# Revit family: Sewage_Removal_System-Zoeller-202_Qwik_Jon_Ultima
name_source: partatom
category: Mechanical Equipment
revit_build: Autodesk Revit 2014 (Build: 20130308_1515(x64)
units: mm (PartAtom-declared; Revit-internal decimal feet)

## types (1)
- 202 – 115V/7.0amps/60Hz
    ADA Compliant = Yes
    Amps = 7 A
    CW Connection = Yes
    Cap = Engineered Plastic
    Cetification = cCSAus (pump only)
    Cooling = Oil Filled
    Cord Length = 108"
    Cord Type = UL listed neoprene cord and plug
    Default Elevation = 0"
    Description = Economical sewage systems designed for free-standing or built-in installations.
    Discharge Diameter = 1"
    Frequency = 60 Hz
    Gasket = Closed cell tank gasket; Buna-N pump o-rings
    HW Connection = No
    Hardware = Stainless Steel
    Height = 14 1/2"
    Horse Power = 1/2
    Impeller = Engineered Plastic
    Impeller Type = Non-clogging vortex
    Insulation = Class B
    Length = 9"
    Lower Bearing = Ball bearings
    Manufacturer = Zoeller
    Material = Plastic-Zoeller-Engineered Plastic
    Max Flow Rate = 45 GPM
    Max. Operating Temp. = 130°F (54°C)
    Maximum Head = 30'
    Mechanical Seals = Carbon/ceramic
    Model = Qwik Jon Ultima
    Motor Housing = Cast iron
    Motor Protection = Auto reset thermal overload
    Motor Shaft = AISI 1215
    Operation = Automatic
    Phase = 1 Ph
    Price = Prices may vary. Please consult Manufacturer Representative for most up-to-date price list.
    Product Documentation Link = http://cdn.qleapahead.com
    Product Page URL = http://www.zoellerpumps.com
    Pump Housing = Engineered Plastic
    RPM = 3450
    Solids Handling = Grinder
    Tank = ABS
    Type = Pemanent split capacitor
    URL = http://www.zoellerpumps.com
    Upper Bearing = Ball bearing
    Vent Connection = Yes
    Voltage = 115 V
    Waste Connection = Yes
    Waste Connection Diameter = 1 1/2"
    Width = 18 5/8"

## geometry (parser evidence)
native form markers: Sweep x1
no freeform markers — native parametric forms only
